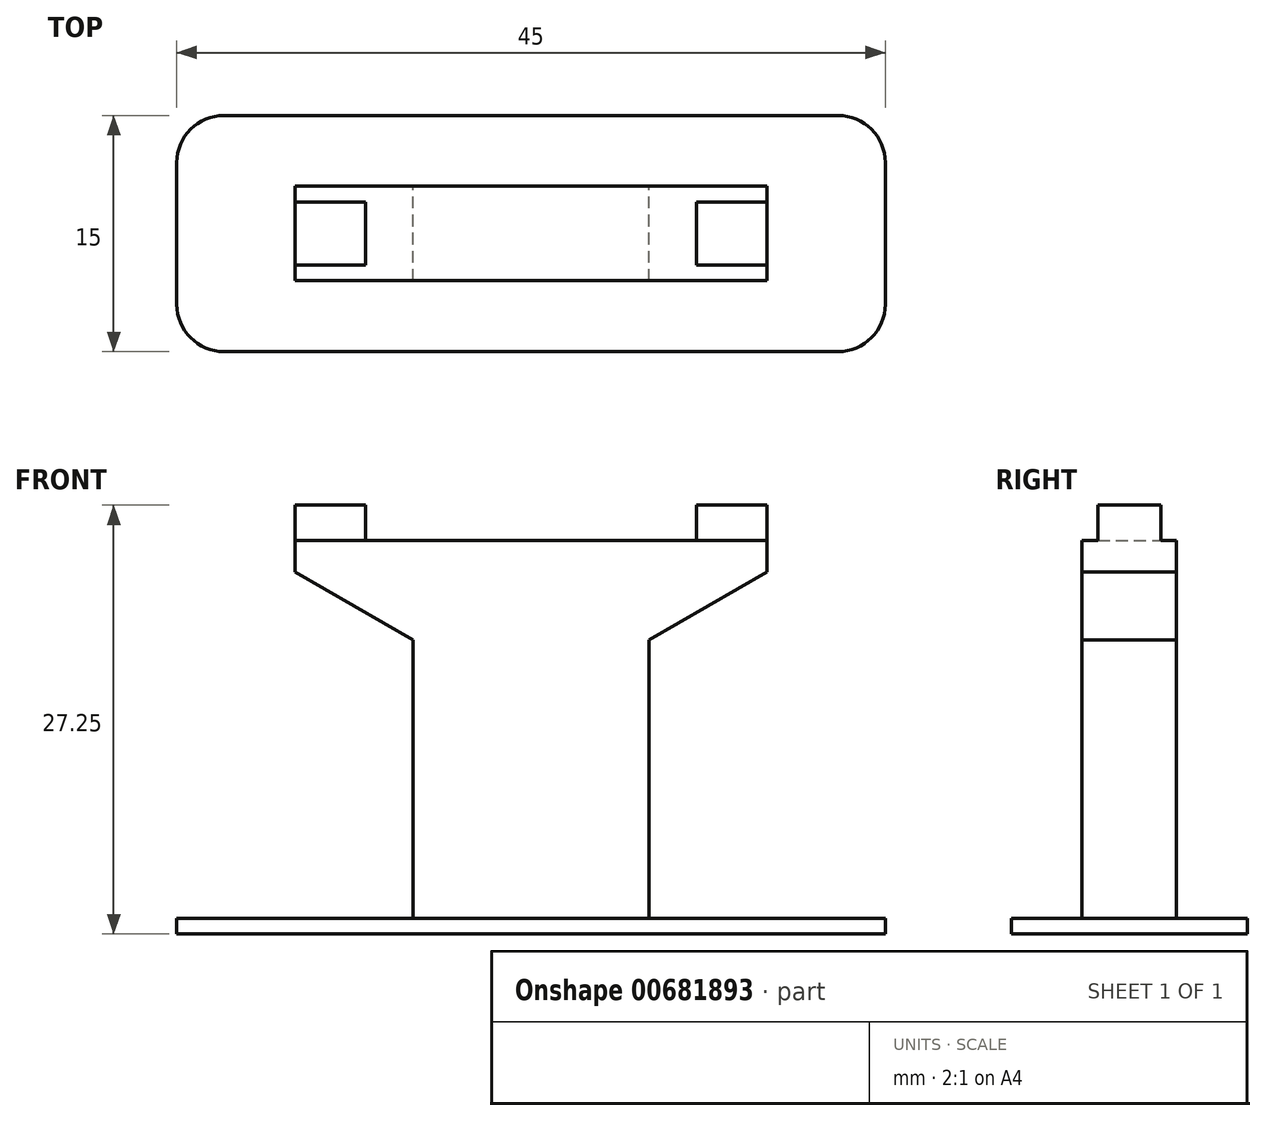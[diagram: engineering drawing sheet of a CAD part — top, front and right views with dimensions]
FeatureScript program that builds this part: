
annotation { "Feature Type Name" : "Feature", "Feature Type Description" : "" }
export const myFeature = defineFeature(function(context is Context, id is Id, definition is map)
    precondition{}
    {
        {
            assignVariable(context, id + "F0", {"name" : "lenght", "anyValue" : 6});
        }
        {
            assignVariable(context, id + "F1", {"name" : "base_lenght", "anyValue" : 15});
        }
        {
            assignVariable(context, id + "F2", {"name" : "track_lenght", "anyValue" : 4});
        }
        {
            var Q0;
            Q0=qCreatedBy(makeId("Front.planeOp"),FACE);
            var sketch = newSketch(context, id + "F3", { "sketchPlane" : qUnion([Q0])});
            skLineSegment(sketch, "E0.bottom", {"start": v(-22.5, 0) * mm, "end": v(22.5, 0) * mm});
            skLineSegment(sketch, "E0.top", {"start": v(-22.5, 1) * mm, "end": v(-7.5, 1) * mm});
            skLineSegment(sketch, "E0.left", {"start": v(-22.5, 0) * mm, "end": v(-22.5, 1) * mm});
            skLineSegment(sketch, "E0.right", {"start": v(22.5, 0) * mm, "end": v(22.5, 1) * mm});
            skLineSegment(sketch, "E1.left", {"start": v(7.5, 1) * mm, "end": v(7.5, 18.67) * mm});
            skLineSegment(sketch, "E1.right", {"start": v(-7.5, 1) * mm, "end": v(-7.5, 18.67) * mm});
            skLineSegment(sketch, "E2", {"start": v(-7.5, 18.67) * mm, "end": v(-15, 23) * mm});
            skLineSegment(sketch, "E3", {"start": v(-15, 23) * mm, "end": v(-15, 27.25) * mm});
            skLineSegment(sketch, "E4", {"start": v(-15, 27.25) * mm, "end": v(-10.5, 27.25) * mm});
            skLineSegment(sketch, "E5", {"start": v(-10.5, 27.25) * mm, "end": v(-10.5, 25) * mm});
            skLineSegment(sketch, "E6", {"start": v(-10.5, 25) * mm, "end": v(10.5, 25) * mm});
            skLineSegment(sketch, "E7", {"start": v(10.5, 25) * mm, "end": v(10.5, 27.25) * mm});
            skLineSegment(sketch, "E8", {"start": v(10.5, 27.25) * mm, "end": v(15, 27.25) * mm});
            skLineSegment(sketch, "E9", {"start": v(15, 27.25) * mm, "end": v(15, 23) * mm});
            skLineSegment(sketch, "E10", {"start": v(15, 23) * mm, "end": v(7.5, 18.67) * mm});
            skLineSegment(sketch, "E11.trimOffspring", {"start": v(7.5, 1) * mm, "end": v(22.5, 1) * mm});
            skLineSegment(sketch, "E12", {"start": v(0, 0) * mm, "end": v(0, 25) * mm, "construction": true});
            skPoint(sketch, "E13", {"position": v(0, 25) * mm});
            skLineSegment(sketch, "E14", {"start": v(7.5, 18.67) * mm, "end": v(-7.5, 18.67) * mm, "construction": true});
            skLineSegment(sketch, "E15", {"start": v(-15, 23) * mm, "end": v(15, 23) * mm, "construction": true});
            skLineSegment(sketch, "E16", {"start": v(15, 27.25) * mm, "end": v(-15, 27.25) * mm, "construction": true});
            skLineSegment(sketch, "E17", {"start": v(-7.5, 1) * mm, "end": v(7.5, 1) * mm});
            skLineSegment(sketch, "E18", {"start": v(-10.5, 25) * mm, "end": v(-15, 25) * mm});
            skLineSegment(sketch, "E19", {"start": v(-15, 25) * mm, "end": v(10.5, 25) * mm});
            skLineSegment(sketch, "E20", {"start": v(10.5, 25) * mm, "end": v(15, 25) * mm});
            skSolve(sketch);
        }
        {
            var Q0;
            Q0=makeQuery(id+"F3.imprint","IMPRINT",FACE,{"disambiguationData":[TD([[makeQuery(id+"F3.imprint","IMPRINT",EDGE,{"derivedFrom":sQuery(id+"F3.wireOp",EDGE,"E1.left")}),1.0]])]});
            extrude(context, id + "F4", {"entities" : qUnion([Q0]), "endBound" : BoundingType.SYMMETRIC, "depth" : (getVariable(context, 'lenght')) * mm, "offsetDistance" : 25 * mm});
        }
        {
            var Q0;
            Q0=makeQuery(id+"F3.imprint","IMPRINT",FACE,{"disambiguationData":[TD([[makeQuery(id+"F3.imprint","IMPRINT",EDGE,{"derivedFrom":sQuery(id+"F3.wireOp",EDGE,"E0.bottom")}),1.0]])]});
            extrude(context, id + "F5", {"entities" : qUnion([Q0]), "operationType" : NewBodyOperationType.ADD, "endBound" : BoundingType.SYMMETRIC, "depth" : (getVariable(context, 'base_lenght')) * mm, "offsetDistance" : 25 * mm});
        }
        {
            var Q0;
            Q0=makeQuery(id+"F3.imprint","IMPRINT",FACE,{"disambiguationData":[TD([[makeQuery(id+"F3.imprint","IMPRINT",EDGE,{"derivedFrom":sQuery(id+"F3.wireOp",EDGE,"E7")}),-1.0]])]});
            var Q1;
            {var subQ0=sQuery(id+"F3.wireOp",EDGE,"E4");Q1=makeQuery(id+"F3.imprint","IMPRINT",FACE,{"disambiguationData":[TD([[makeQuery(id+"F3.imprint","IMPRINT",EDGE,{"derivedFrom":subQ0}),-1.0]])]});}
            extrude(context, id + "F6", {"entities" : qUnion([Q0, Q1]), "operationType" : NewBodyOperationType.ADD, "endBound" : BoundingType.SYMMETRIC, "depth" : (getVariable(context, 'track_lenght')) * mm, "offsetDistance" : 25 * mm});
        }
        {
            var Q0;
            Q0=makeQuery(id+"F5.opExtrude","CAP_EDGE",EDGE,{"disambiguationData":[OSD([sQuery(id+"F3.wireOp",EDGE,"E0.right")])],"isStart":false});
            var Q1;
            Q1=makeQuery(id+"F5.opExtrude","CAP_EDGE",EDGE,{"disambiguationData":[OSD([sQuery(id+"F3.wireOp",EDGE,"E0.right")])],"isStart":true});
            var Q2;
            Q2=makeQuery(id+"F5.opExtrude","CAP_EDGE",EDGE,{"disambiguationData":[OSD([sQuery(id+"F3.wireOp",EDGE,"E0.left")])],"isStart":true});
            var Q3;
            Q3=makeQuery(id+"F5.opExtrude","CAP_EDGE",EDGE,{"disambiguationData":[OSD([sQuery(id+"F3.wireOp",EDGE,"E0.left")])],"isStart":false});
            fillet(context, id + "F7", {"entities" : qUnion([Q0, Q1, Q2, Q3]), "radius" : 3 * mm, "tangentPropagation" : true, "allowEdgeOverflow" : false});
        }
    });
